FCSTD DOCUMENT  (FreeCAD 0.15R4671 (Git))
Label: calibpattern_cone
License: All rights reserved
LicenseURL: http://en.wikipedia.org/wiki/All_rights_reserved
objects: Sketcher::SketchObject×1
note: 1 computed .brp shape members not serialized (recipe doc carries the construction recipe); baked Part::Feature solids carry a one-line shape summary decoded from their .brp

FEATURE [Sketcher::SketchObject] Sketch
  sketch-geometry (19):
    g0: LineSegment StartX=-98.7947 StartY=-46.6831 StartZ=0 EndX=-78.8751 EndY=68.9132 EndZ=0
    g1: LineSegment StartX=-98.7947 StartY=-46.6831 StartZ=0 EndX=-114.668 EndY=-162.904 EndZ=0
    g2: LineSegment StartX=-98.7947 StartY=-46.6831 StartZ=0 EndX=-94.3285 EndY=-20.7651 EndZ=0
    g3: LineSegment StartX=-98.7947 StartY=-46.6831 StartZ=0 EndX=-102.354 EndY=-72.7412 EndZ=0
    g4: ArcOfCircle CenterX=-98.7947 CenterY=-46.6831 CenterZ=0 NormalX=0 NormalY=0 NormalZ=1 Radius=117.3 StartAngle=1.40015 EndAngle=4.57665
    g5: ArcOfCircle CenterX=-98.7947 CenterY=-46.6831 CenterZ=0 NormalX=0 NormalY=0 NormalZ=1 Radius=26.3 StartAngle=1.40015 EndAngle=4.57665
    g6: ArcOfCircle CenterX=-98.7947 CenterY=-46.6831 CenterZ=0 NormalX=0 NormalY=0 NormalZ=1 Radius=39 StartAngle=1.40015 EndAngle=4.57665
    g7: ArcOfCircle CenterX=-98.7947 CenterY=-46.6831 CenterZ=0 NormalX=0 NormalY=0 NormalZ=1 Radius=52 StartAngle=1.40015 EndAngle=4.57665
    g8: ArcOfCircle CenterX=-98.7947 CenterY=-46.6831 CenterZ=0 NormalX=0 NormalY=0 NormalZ=1 Radius=65 StartAngle=1.40015 EndAngle=4.57665
    g9: ArcOfCircle CenterX=-98.7947 CenterY=-46.6831 CenterZ=0 NormalX=0 NormalY=0 NormalZ=1 Radius=78 StartAngle=1.40015 EndAngle=4.57665
    g10: ArcOfCircle CenterX=-98.7947 CenterY=-46.6831 CenterZ=0 NormalX=0 NormalY=0 NormalZ=1 Radius=91 StartAngle=1.40015 EndAngle=4.57665
    g11: ArcOfCircle CenterX=-98.7947 CenterY=-46.6831 CenterZ=0 NormalX=0 NormalY=0 NormalZ=1 Radius=104 StartAngle=1.40015 EndAngle=4.57665
    g12: LineSegment StartX=-98.7947 StartY=-46.6831 StartZ=0 EndX=-158.377 EndY=-147.724 EndZ=0
    g13: LineSegment StartX=-98.7947 StartY=-46.6831 StartZ=0 EndX=-192.815 EndY=-116.822 EndZ=0
    g14: LineSegment StartX=-98.7947 StartY=-46.6831 StartZ=0 EndX=-212.624 EndY=-75.0065 EndZ=0
    g15: LineSegment StartX=-98.7947 StartY=-46.6831 StartZ=0 EndX=-214.721 EndY=-28.784 EndZ=0
    g16: LineSegment StartX=-98.7947 StartY=-46.6831 StartZ=0 EndX=-198.78 EndY=14.6535 EndZ=0
    g17: LineSegment StartX=-98.7947 StartY=-46.6831 StartZ=0 EndX=-167.282 EndY=48.5471 EndZ=0
    g18: LineSegment StartX=-98.7947 StartY=-46.6831 StartZ=0 EndX=-125.127 EndY=67.623 EndZ=0
  constraints (61):
    c: Coincident(g1,g0)
    c: Equal(g0,g1)
    c: Distance(g0) = 117.3
    c: Angle(g1,g0) = 3.10669
    c: Coincident(g2,g0)
    c: Coincident(g3,g0)
    c: Equal(g2,g3)
    c: Angle(g3,g2) = 3.10669
    c: Distance(g2) = 26.3
    c: PointOnObject(g2,g0)
    c: Coincident(g4,g0)
    c: Coincident(g4,g0)
    c: Coincident(g4,g1)
    c: Coincident(g5,g0)
    c: Coincident(g5,g2)
    c: Coincident(g5,g3)
    c: Coincident(g6,g0)
    c: PointOnObject(g6,g0)
    c: PointOnObject(g6,g1)
    c: Radius(g6) = 39
    c: Coincident(g7,g0)
    c: PointOnObject(g7,g0)
    c: PointOnObject(g7,g1)
    c: Radius(g7) = 52
    c: Coincident(g8,g0)
    c: PointOnObject(g8,g0)
    c: PointOnObject(g8,g1)
    c: Radius(g8) = 65
    c: Coincident(g9,g0)
    c: PointOnObject(g9,g0)
    c: PointOnObject(g9,g1)
    c: Radius(g9) = 78
    c: Coincident(g10,g0)
    c: PointOnObject(g10,g0)
    c: PointOnObject(g10,g1)
    c: Radius(g10) = 91
    c: Coincident(g11,g0)
    c: PointOnObject(g11,g0)
    c: PointOnObject(g11,g1)
    c: Radius(g11) = 104
    c: Coincident(g12,g0)
    c: PointOnObject(g12,g4)
    c: Angle(g12,g1) = 0.397062
    c: Coincident(g13,g0)
    c: PointOnObject(g13,g4)
    c: Angle(g13,g1) = 0.794125
    c: Coincident(g14,g0)
    c: PointOnObject(g14,g4)
    c: Angle(g14,g1) = 1.19119
    c: Coincident(g15,g0)
    c: PointOnObject(g15,g4)
    c: Coincident(g16,g0)
    c: PointOnObject(g16,g4)
    c: Angle(g15,g1) = 1.58825
    c: Angle(g16,g1) = 1.98531
    c: Coincident(g17,g0)
    c: PointOnObject(g17,g4)
    c: Angle(g17,g1) = 2.38237
    c: Coincident(g18,g0)
    c: PointOnObject(g18,g4)
    c: Angle(g18,g1) = 2.77944
